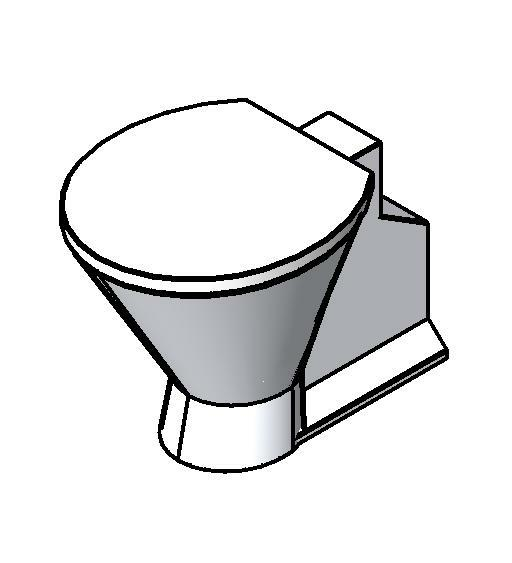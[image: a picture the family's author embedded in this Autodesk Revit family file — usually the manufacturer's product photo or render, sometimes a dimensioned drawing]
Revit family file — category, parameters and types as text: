
# Revit family: Deca_Cuba sobrepor redonda 30cm _Cuba Slim_L.22030
name_source: partatom
category: Plumbing Fixtures
units: mm (PartAtom-declared; Revit-internal decimal feet)

## family parameters
Cut with Voids When Loaded = No
Host = Face
Part Type = Normal
Room Calculation Point = No
Round Connector Dimension = Use Radius
Shared = No

## types (5) — shared parameters
Acompanha o Produto = Acabamento da válvula cerâmica/Smartblock
Aprovado por = quattroD
Atendimento ao Cliente = 0800-0117073
Categoria = CUBAS
Composição Básica = Composição Básica: Argila / Feldispato / Caulim / Vidrados e corantes inorgânicos / Plásticos de Engenharia.
Composição Componente = PEBD
Cores Componente = transparente
Criado por = quattroD
Código Pai = L.22030.17
Linha = CUBA SLIM
Manufacturer = DECA
Norma = NBR 16728-1 / NBR 16728-2
Peso Líquido (Kg) = 5.2
Pressão máx. funcionamento = 40mca
Pressão mín. funcionamento = 3mca
Saída de Esgoto = válvula curta
Segmento = LUXO
URL = www.deca.com.br
zero-valued in all types: CWFU, Default Elevation, Diâmetro Ponto de Esgoto, Diâmetro Água Fria, Raio Ponto de Esgoto, Raio Água Fria, WFU

## per-type parameters (varying)
| type | Cor Interna | Cor Principal | Informações Complementares | Material | Model |
| L.22030.17_Branco | Branco | Branco | Esmalte Protekto | Deca_Branco | L.22030.17 |
| L.22030.26_Barbante | Barbante | Barbante |  | Deca_Barbante | L.22030.26 |
| L.22030.49_Sálvia | Sálvia | Sálvia |  | Deca_Sálvia | L.22030.49 |
| L.22030.85_Cinza Antracite | Cinza Soft Antracite | Antracite |  | Deca_Cinza Antracite | L.22030.85 |
| L.22030.94_Ébano Fosco | Ébano Fosco | Ébano Fosco |  | Deca_Ébano Fosco | L.22030.94 |

## geometry (parser evidence)
native form markers: Sweep x3
no freeform markers — native parametric forms only
